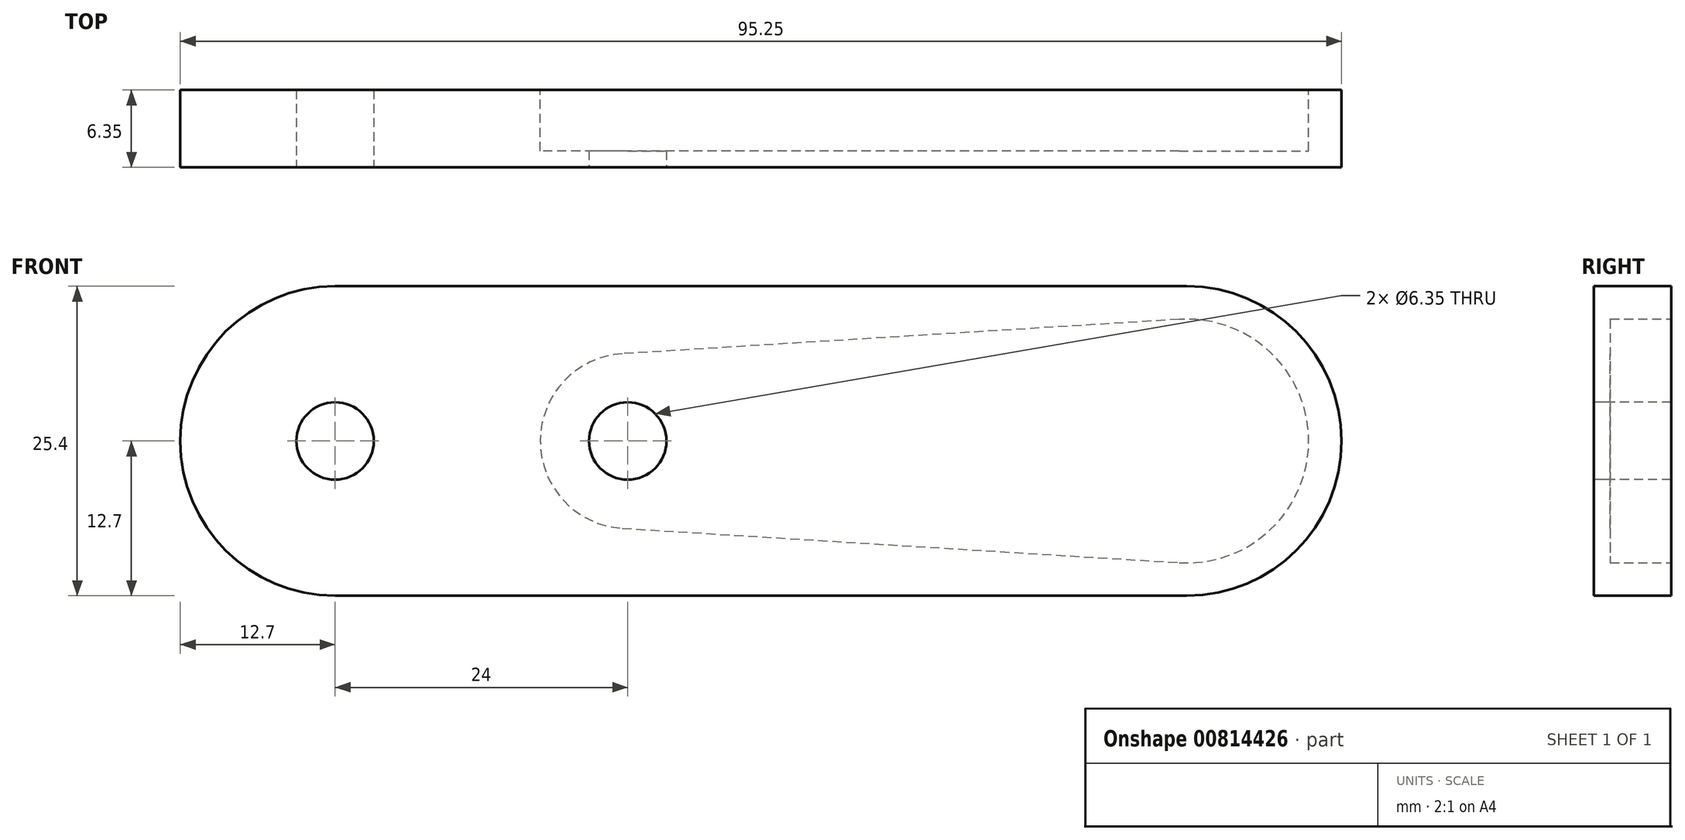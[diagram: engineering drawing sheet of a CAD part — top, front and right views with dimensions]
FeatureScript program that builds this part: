
annotation { "Feature Type Name" : "Feature", "Feature Type Description" : "" }
export const myFeature = defineFeature(function(context is Context, id is Id, definition is map)
    precondition{}
    {
        {
            var Q0;
            Q0=qCreatedBy(makeId("Front.planeOp"),FACE);
            var sketch = newSketch(context, id + "F0", { "sketchPlane" : qUnion([Q0])});
            skLineSegment(sketch, "E0.bottom", {"start": v(0, 12.7) * mm, "end": v(69.85, 12.7) * mm});
            skLineSegment(sketch, "E0.top", {"start": v(0, -12.7) * mm, "end": v(69.85, -12.7) * mm});
            skArc(sketch, "E1", {"start": v(0, 12.7) * mm, "mid": v(-12.7, 0) * mm, "end": v(0, -12.7) * mm});
            skArc(sketch, "E2", {"start": v(69.85, -12.7) * mm, "mid": v(82.55, 0) * mm, "end": v(69.85, 12.7) * mm});
            skSolve(sketch);
        }
        {
            var Q0;
            Q0 = qSketchRegion(id + "F0", true);
            extrude(context, id + "F1", {"entities" : qUnion([Q0]), "depth" : 6.35 * mm, "offsetDistance" : 25 * mm});
        }
        {
            var Q0;
            Q0=makeQuery(id+"F1.opExtrude","CAP_FACE",FACE,{"disambiguationData":[OSD([sQuery(id+"F0.wireOp",EDGE,"E0.bottom"),sQuery(id+"F0.wireOp",EDGE,"E0.top"),sQuery(id+"F0.wireOp",EDGE,"E1"),sQuery(id+"F0.wireOp",EDGE,"E2")])],"isStart":false});
            var sketch = newSketch(context, id + "F2", { "sketchPlane" : qUnion([Q0])});
            skCircle(sketch, "E3", {"center": v(0, 0) * mm, "radius": 3.17 * mm});
            skCircle(sketch, "E4", {"center": v(24, 0) * mm, "radius": 3.17 * mm});
            skPoint(sketch, "E4.centerSnap0", {"position": v(-12.7, 0) * mm});
            skSolve(sketch);
        }
        {
            var Q0;
            Q0 = qSketchRegion(id + "F2", true);
            extrude(context, id + "F3", {"entities" : qUnion([Q0]), "operationType" : NewBodyOperationType.REMOVE, "endBound" : BoundingType.UP_TO_NEXT, "oppositeDirection" : true, "depth" : 25 * mm, "offsetDistance" : 25 * mm});
        }
        {
            var Q0;
            Q0=makeQuery(id+"F1.opExtrude","CAP_FACE",FACE,{"disambiguationData":[OSD([sQuery(id+"F0.wireOp",EDGE,"E0.bottom"),sQuery(id+"F0.wireOp",EDGE,"E0.top"),sQuery(id+"F0.wireOp",EDGE,"E1"),sQuery(id+"F0.wireOp",EDGE,"E2")])],"isStart":true});
            var sketch = newSketch(context, id + "F4", { "sketchPlane" : qUnion([Q0])});
            skArc(sketch, "E5", {"start": v(-69.23, 9.98) * mm, "mid": v(-79.85, 0) * mm, "end": v(-69.23, -9.98) * mm});
            skArc(sketch, "E6", {"start": v(-23.56, -7.16) * mm, "mid": v(-16.82, 0) * mm, "end": v(-23.56, 7.16) * mm});
            skLineSegment(sketch, "E7", {"start": v(-69.23, 9.98) * mm, "end": v(-23.56, 7.16) * mm});
            skLineSegment(sketch, "E8", {"start": v(-23.56, -7.16) * mm, "end": v(-69.23, -9.98) * mm});
            skSolve(sketch);
        }
        {
            var Q0;
            Q0 = qSketchRegion(id + "F4", true);
            extrude(context, id + "F5", {"entities" : qUnion([Q0]), "operationType" : NewBodyOperationType.REMOVE, "oppositeDirection" : true, "depth" : 5 * mm, "offsetDistance" : 25 * mm});
        }
    });
